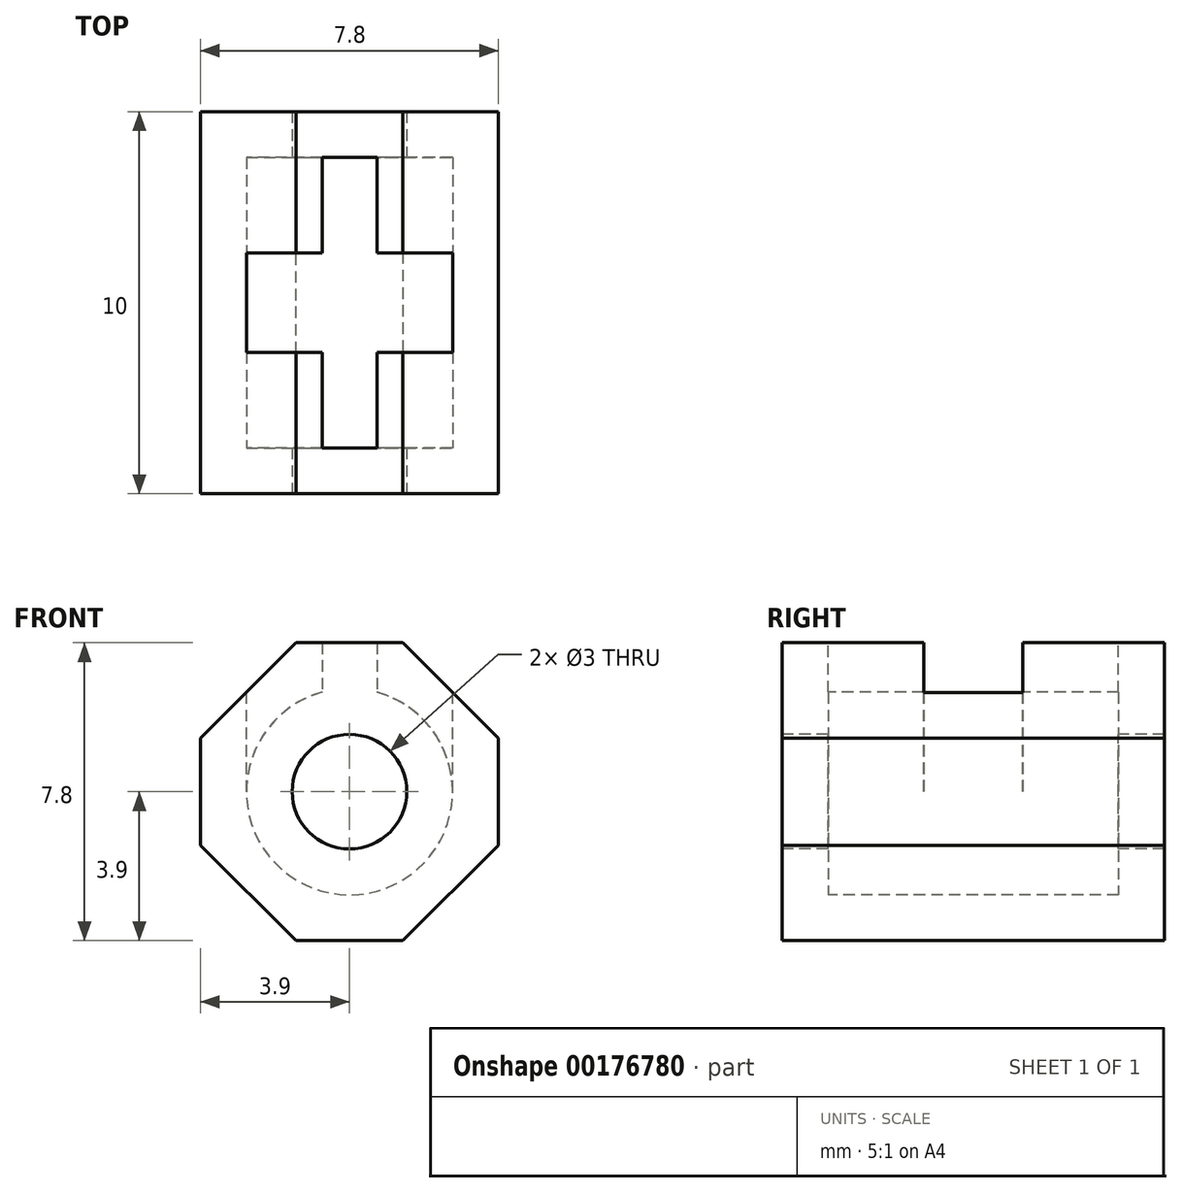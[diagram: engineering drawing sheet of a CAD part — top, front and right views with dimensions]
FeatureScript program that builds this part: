
annotation { "Feature Type Name" : "Feature", "Feature Type Description" : "" }
export const myFeature = defineFeature(function(context is Context, id is Id, definition is map)
    precondition{}
    {
        {
            assignVariable(context, id + "F0", {"name" : "standOffHeight", "anyValue" : 10 * mm});
        }
        {
            assignVariable(context, id + "F1", {"name" : "screwHeadDiameter", "anyValue" : 5.4 * mm});
        }
        {
            assignVariable(context, id + "F2", {"name" : "defaultThickness", "anyValue" : 1.2 * mm});
        }
        {
            var Q0;
            Q0=qCreatedBy(makeId("Top.planeOp"),FACE);
            var sketch = newSketch(context, id + "F3", { "sketchPlane" : qUnion([Q0])});
            skLineSegment(sketch, "E0.bottom", {"start": v(-3.9, 5) * mm, "end": v(3.9, 5) * mm});
            skLineSegment(sketch, "E0.top", {"start": v(-3.9, -5) * mm, "end": v(3.9, -5) * mm});
            skLineSegment(sketch, "E0.left", {"start": v(-3.9, 5) * mm, "end": v(-3.9, -5) * mm});
            skLineSegment(sketch, "E0.right", {"start": v(3.9, 5) * mm, "end": v(3.9, -5) * mm});
            skPoint(sketch, "E0.middle", {"position": v(0, 0) * mm});
            skLineSegment(sketch, "E1.bottom", {"start": v(-2.7, 1.3) * mm, "end": v(2.7, 1.3) * mm});
            skLineSegment(sketch, "E1.top", {"start": v(-2.7, -1.3) * mm, "end": v(2.7, -1.3) * mm});
            skLineSegment(sketch, "E1.left", {"start": v(-2.7, 1.3) * mm, "end": v(-2.7, -1.3) * mm});
            skLineSegment(sketch, "E1.right", {"start": v(2.7, 1.3) * mm, "end": v(2.7, -1.3) * mm});
            skSolve(sketch);
        }
        {
            var Q0;
            Q0=makeQuery(id+"F3.imprint","IMPRINT",FACE,{"disambiguationData":[TD([[makeQuery(id+"F3.imprint","IMPRINT",EDGE,{"derivedFrom":sQuery(id+"F3.wireOp",EDGE,"E0.bottom")}),-1.0]])]});
            var Q1;
            Q1=makeQuery(id+"F3.imprint","IMPRINT",FACE,{"disambiguationData":[TD([[makeQuery(id+"F3.imprint","IMPRINT",EDGE,{"derivedFrom":sQuery(id+"F3.wireOp",EDGE,"E1.bottom")}),-1.0]])]});
            extrude(context, id + "F4", {"entities" : qUnion([Q0, Q1]), "depth" : getVariable(context, 'screwHeadDiameter') + (getVariable(context, 'defaultThickness') * 2), "offsetDistance" : 25 * mm});
        }
        {
            var Q0;
            Q0=makeQuery(id+"F4.opExtrude","SWEPT_FACE",FACE,{"disambiguationData":[OSD([sQuery(id+"F3.wireOp",EDGE,"E0.top")])]});
            cPlane(context, id + "F5", {"entities" : qUnion([Q0]), "cplaneType" : CPlaneType.OFFSET, "offset" : getVariable(context, 'standOffHeight') / 2, "oppositeDirection" : true, "width" : 150 * mm, "height" : 150 * mm});
        }
        {
            var Q0;
            Q0=qCreatedBy(id+"F5.planeOp",FACE);
            var sketch = newSketch(context, id + "F6", { "sketchPlane" : qUnion([Q0])});
            skCircle(sketch, "E2", {"center": v(0, 3.9) * mm, "radius": 2.7 * mm});
            skLineSegment(sketch, "E3", {"start": v(0, 0) * mm, "end": v(0, 3.9) * mm});
            skLineSegment(sketch, "E4", {"start": v(0, 3.9) * mm, "end": v(0, 7.8) * mm});
            skSolve(sketch);
        }
        {
            var Q0;
            Q0 = qSketchRegion(id + "F6", true);
            extrude(context, id + "F7", {"entities" : qUnion([Q0]), "operationType" : NewBodyOperationType.REMOVE, "oppositeDirection" : true, "depth" : (getVariable(context, 'standOffHeight') / 2) - getVariable(context, 'defaultThickness'), "offsetDistance" : 25 * mm, "hasSecondDirection" : true, "secondDirectionOppositeDirection" : false, "secondDirectionDepth" : (getVariable(context, 'standOffHeight') / 2) - getVariable(context, 'defaultThickness')});
        }
        {
            var Q0;
            Q0=makeQuery(id+"F4.opExtrude","CAP_FACE",FACE,{"disambiguationData":[OSD([sQuery(id+"F3.wireOp",EDGE,"E0.bottom"),sQuery(id+"F3.wireOp",EDGE,"E0.top"),sQuery(id+"F3.wireOp",EDGE,"E0.left"),sQuery(id+"F3.wireOp",EDGE,"E0.right")])],"isStart":false});
            var sketch = newSketch(context, id + "F8", { "sketchPlane" : qUnion([Q0])});
            skLineSegment(sketch, "E5.bottom", {"start": v(-2.7, 1.3) * mm, "end": v(2.7, 1.3) * mm});
            skLineSegment(sketch, "E5.top", {"start": v(-2.7, -1.3) * mm, "end": v(2.7, -1.3) * mm});
            skLineSegment(sketch, "E5.left", {"start": v(-2.7, 1.3) * mm, "end": v(-2.7, -1.3) * mm});
            skLineSegment(sketch, "E5.right", {"start": v(2.7, 1.3) * mm, "end": v(2.7, -1.3) * mm});
            skPoint(sketch, "E5.middle", {"position": v(0, 0) * mm});
            skSolve(sketch);
        }
        {
            var Q0;
            Q0=makeQuery(id+"F8.imprint","IMPRINT",FACE,{"disambiguationData":[TD([[makeQuery(id+"F8.imprint","IMPRINT",EDGE,{"derivedFrom":sQuery(id+"F8.wireOp",EDGE,"E5.bottom")}),-1.0]])]});
            extrude(context, id + "F9", {"entities" : qUnion([Q0]), "operationType" : NewBodyOperationType.REMOVE, "oppositeDirection" : true, "depth" : getVariable(context, 'screwHeadDiameter') / 2 + getVariable(context, 'defaultThickness'), "offsetDistance" : 25 * mm});
        }
        {
            var Q0;
            Q0=makeQuery(id+"F4.opExtrude","CAP_FACE",FACE,{"disambiguationData":[OSD([sQuery(id+"F3.wireOp",EDGE,"E0.bottom"),sQuery(id+"F3.wireOp",EDGE,"E0.top"),sQuery(id+"F3.wireOp",EDGE,"E0.left"),sQuery(id+"F3.wireOp",EDGE,"E0.right")])],"isStart":false});
            var sketch = newSketch(context, id + "F10", { "sketchPlane" : qUnion([Q0])});
            skLineSegment(sketch, "E6.bottom", {"start": v(-0.72, 3.8) * mm, "end": v(0.72, 3.8) * mm});
            skLineSegment(sketch, "E6.top", {"start": v(-0.72, -3.8) * mm, "end": v(0.72, -3.8) * mm});
            skLineSegment(sketch, "E6.left", {"start": v(-0.72, 3.8) * mm, "end": v(-0.72, -3.8) * mm});
            skLineSegment(sketch, "E6.right", {"start": v(0.72, 3.8) * mm, "end": v(0.72, -3.8) * mm});
            skPoint(sketch, "E6.middle", {"position": v(0, 0) * mm});
            skSolve(sketch);
        }
        {
            var Q0;
            Q0 = qSketchRegion(id + "F10", true);
            extrude(context, id + "F11", {"entities" : qUnion([Q0]), "operationType" : NewBodyOperationType.REMOVE, "oppositeDirection" : true, "depth" : getVariable(context, 'screwHeadDiameter') / 2 + getVariable(context, 'defaultThickness'), "offsetDistance" : 25 * mm});
        }
        {
            var Q0;
            Q0=makeQuery(id+"F4.opExtrude","SWEPT_FACE",FACE,{"disambiguationData":[OSD([sQuery(id+"F3.wireOp",EDGE,"E0.top")])]});
            var sketch = newSketch(context, id + "F12", { "sketchPlane" : qUnion([Q0])});
            skCircle(sketch, "E7", {"center": v(0, 3.9) * mm, "radius": 1.5 * mm});
            skLineSegment(sketch, "E8", {"start": v(0, 7.8) * mm, "end": v(0, 3.9) * mm});
            skLineSegment(sketch, "E9", {"start": v(0, 3.9) * mm, "end": v(0, 0) * mm});
            skSolve(sketch);
        }
        {
            var Q0;
            Q0 = qSketchRegion(id + "F12", true);
            extrude(context, id + "F13", {"entities" : qUnion([Q0]), "operationType" : NewBodyOperationType.REMOVE, "endBound" : BoundingType.THROUGH_ALL, "oppositeDirection" : true, "depth" : 25 * mm, "offsetDistance" : 25 * mm});
        }
        {
            var Q0;
            Q0=makeQuery(id+"F4.opExtrude","CAP_EDGE",EDGE,{"disambiguationData":[OSD([sQuery(id+"F3.wireOp",EDGE,"E0.left")])],"isStart":false});
            var Q1;
            Q1=makeQuery(id+"F4.opExtrude","CAP_EDGE",EDGE,{"disambiguationData":[OSD([sQuery(id+"F3.wireOp",EDGE,"E0.left")])],"isStart":true});
            var Q2;
            Q2=makeQuery(id+"F4.opExtrude","CAP_EDGE",EDGE,{"disambiguationData":[OSD([sQuery(id+"F3.wireOp",EDGE,"E0.right")])],"isStart":true});
            var Q3;
            Q3=makeQuery(id+"F4.opExtrude","CAP_EDGE",EDGE,{"disambiguationData":[OSD([sQuery(id+"F3.wireOp",EDGE,"E0.right")])],"isStart":false});
            chamfer(context, id + "F14", {"entities" : qUnion([Q0, Q1, Q2, Q3]), "width" : 2.5 * mm, "tangentPropagation" : true});
        }
    });
